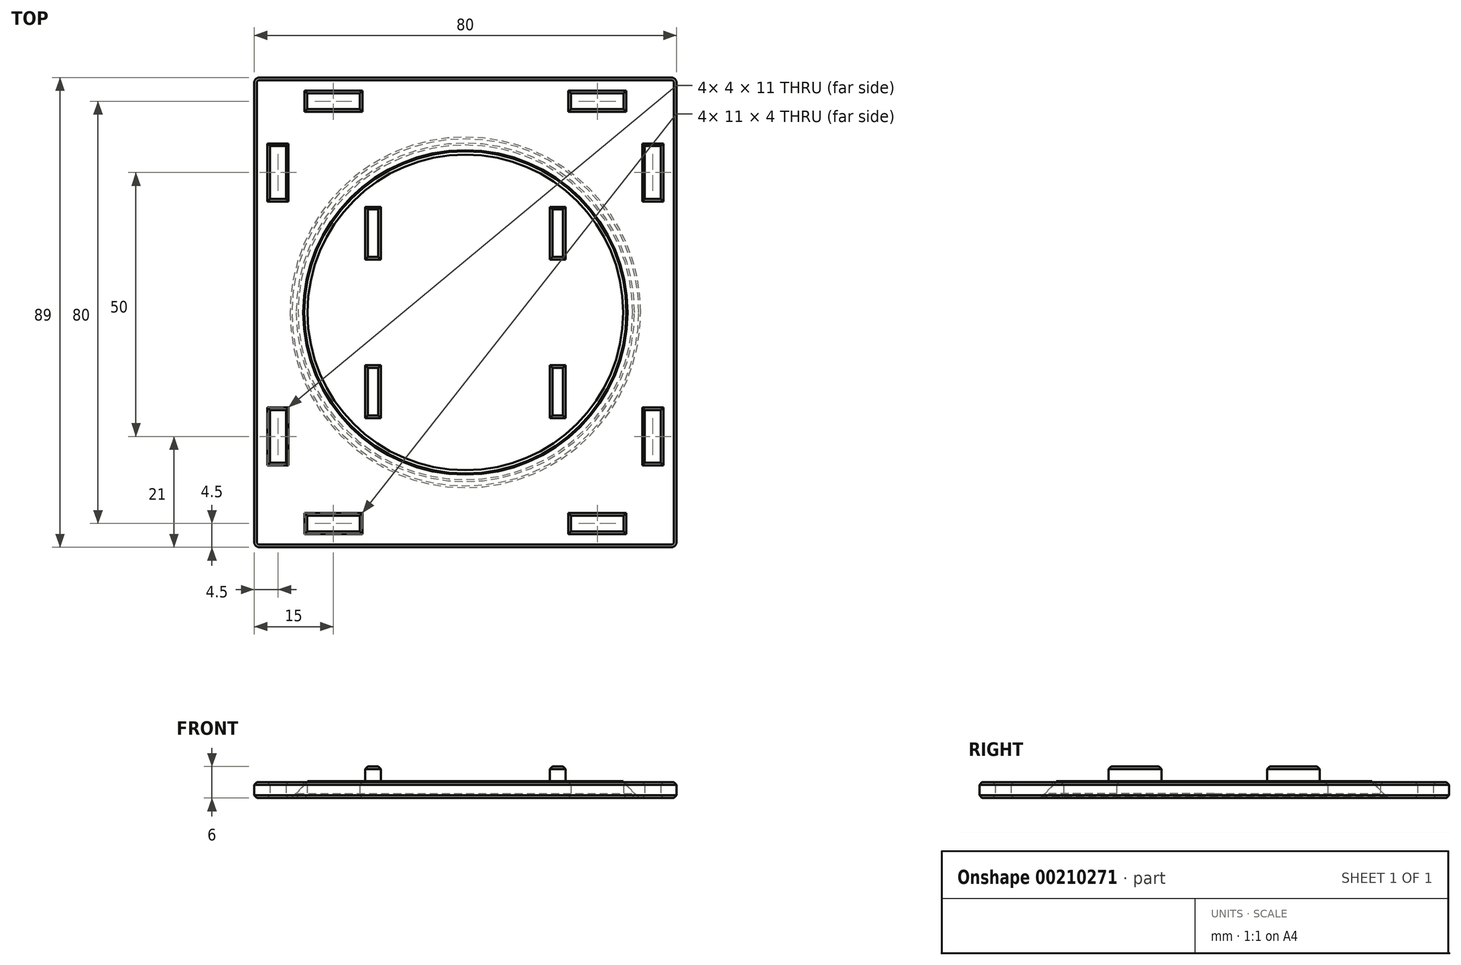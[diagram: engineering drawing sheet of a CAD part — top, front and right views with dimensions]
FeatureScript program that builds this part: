
annotation { "Feature Type Name" : "Feature", "Feature Type Description" : "" }
export const myFeature = defineFeature(function(context is Context, id is Id, definition is map)
    precondition{}
    {
        {
            var Q0;
            Q0=qCreatedBy(makeId("Top.planeOp"),FACE);
            var sketch = newSketch(context, id + "F0", { "sketchPlane" : qUnion([Q0])});
            skLineSegment(sketch, "E0.bottom", {"start": v(0, 0) * mm, "end": v(80, 0) * mm});
            skLineSegment(sketch, "E0.top", {"start": v(0, 89) * mm, "end": v(80, 89) * mm});
            skLineSegment(sketch, "E0.left", {"start": v(0, 0) * mm, "end": v(0, 89) * mm});
            skLineSegment(sketch, "E0.right", {"start": v(80, 0) * mm, "end": v(80, 89) * mm});
            skLineSegment(sketch, "E1.bottom", {"start": v(3, 76) * mm, "end": v(6, 76) * mm});
            skLineSegment(sketch, "E1.top", {"start": v(3, 66) * mm, "end": v(6, 66) * mm});
            skLineSegment(sketch, "E1.left", {"start": v(3, 76) * mm, "end": v(3, 66) * mm});
            skLineSegment(sketch, "E1.right", {"start": v(6, 76) * mm, "end": v(6, 66) * mm});
            skLineSegment(sketch, "E2.0.1.0", {"start": v(3, 26) * mm, "end": v(6, 26) * mm});
            skLineSegment(sketch, "E2.0.1.1", {"start": v(6, 26) * mm, "end": v(6, 16) * mm});
            skLineSegment(sketch, "E2.0.1.2", {"start": v(3, 26) * mm, "end": v(3, 16) * mm});
            skLineSegment(sketch, "E2.0.1.3", {"start": v(3, 16) * mm, "end": v(6, 16) * mm});
            skLineSegment(sketch, "E2.1.0.0", {"start": v(74, 76) * mm, "end": v(77, 76) * mm});
            skLineSegment(sketch, "E2.1.0.1", {"start": v(77, 76) * mm, "end": v(77, 66) * mm});
            skLineSegment(sketch, "E2.1.0.2", {"start": v(74, 76) * mm, "end": v(74, 66) * mm});
            skLineSegment(sketch, "E2.1.0.3", {"start": v(74, 66) * mm, "end": v(77, 66) * mm});
            skLineSegment(sketch, "E2.1.1.0", {"start": v(74, 26) * mm, "end": v(77, 26) * mm});
            skLineSegment(sketch, "E2.1.1.1", {"start": v(77, 26) * mm, "end": v(77, 16) * mm});
            skLineSegment(sketch, "E2.1.1.2", {"start": v(74, 26) * mm, "end": v(74, 16) * mm});
            skLineSegment(sketch, "E2.1.1.3", {"start": v(74, 16) * mm, "end": v(77, 16) * mm});
            skLineSegment(sketch, "E2.direction1", {"start": v(3, 76) * mm, "end": v(74, 76) * mm, "construction": true});
            skLineSegment(sketch, "E2.direction2", {"start": v(3, 76) * mm, "end": v(3, 26) * mm, "construction": true});
            skCircle(sketch, "E3", {"center": v(40, 44.5) * mm, "radius": 30 * mm});
            skPoint(sketch, "E3.centerSnap0", {"position": v(80, 44.5) * mm});
            skPoint(sketch, "E3.centerSnap1", {"position": v(40, 89) * mm});
            skLineSegment(sketch, "E4.bottom", {"start": v(70, 3) * mm, "end": v(60, 3) * mm});
            skLineSegment(sketch, "E4.top", {"start": v(70, 6) * mm, "end": v(60, 6) * mm});
            skLineSegment(sketch, "E4.left", {"start": v(70, 3) * mm, "end": v(70, 6) * mm});
            skLineSegment(sketch, "E4.right", {"start": v(60, 3) * mm, "end": v(60, 6) * mm});
            skLineSegment(sketch, "E5.0.1.0", {"start": v(70, 83) * mm, "end": v(60, 83) * mm});
            skLineSegment(sketch, "E5.0.1.1", {"start": v(60, 83) * mm, "end": v(60, 86) * mm});
            skLineSegment(sketch, "E5.0.1.2", {"start": v(70, 86) * mm, "end": v(60, 86) * mm});
            skLineSegment(sketch, "E5.0.1.3", {"start": v(70, 83) * mm, "end": v(70, 86) * mm});
            skLineSegment(sketch, "E5.1.0.0", {"start": v(20, 3) * mm, "end": v(10, 3) * mm});
            skLineSegment(sketch, "E5.1.0.1", {"start": v(10, 3) * mm, "end": v(10, 6) * mm});
            skLineSegment(sketch, "E5.1.0.2", {"start": v(20, 6) * mm, "end": v(10, 6) * mm});
            skLineSegment(sketch, "E5.1.0.3", {"start": v(20, 3) * mm, "end": v(20, 6) * mm});
            skLineSegment(sketch, "E5.1.1.0", {"start": v(20, 83) * mm, "end": v(10, 83) * mm});
            skLineSegment(sketch, "E5.1.1.1", {"start": v(10, 83) * mm, "end": v(10, 86) * mm});
            skLineSegment(sketch, "E5.1.1.2", {"start": v(20, 86) * mm, "end": v(10, 86) * mm});
            skLineSegment(sketch, "E5.1.1.3", {"start": v(20, 83) * mm, "end": v(20, 86) * mm});
            skLineSegment(sketch, "E5.direction1", {"start": v(60, 3) * mm, "end": v(10, 3) * mm, "construction": true});
            skLineSegment(sketch, "E5.direction2", {"start": v(60, 3) * mm, "end": v(60, 83) * mm, "construction": true});
            skSolve(sketch);
        }
        {
            var Q0;
            Q0=qSketchRegion(id+"F0",true);
            extrude(context, id + "F1", {"entities" : qUnion([Q0]), "depth" : 3 * mm});
        }
        {
            var Q0;
            Q0=makeQuery(id+"F1.opExtrude","CAP_EDGE",EDGE,{"disambiguationData":[OSD([sQuery(id+"F0.wireOp",EDGE,"E3")])],"isStart":true});
            chamfer(context, id + "F2", {"entities" : qUnion([Q0]), "width" : 3 * mm, "tangentPropagation" : true});
        }
        {
            var Q0;
            Q0=qCreatedBy(makeId("Top.planeOp"),FACE);
            var sketch = newSketch(context, id + "F3", { "sketchPlane" : qUnion([Q0])});
            skCircle(sketch, "E6", {"center": v(40, 44.5) * mm, "radius": 32.9 * mm});
            skSolve(sketch);
        }
        {
            var Q0;
            Q0=qSketchRegion(id+"F3",true);
            extrude(context, id + "F4", {"entities" : qUnion([Q0]), "depth" : 3 * mm});
        }
        {
            var Q0;
            Q0=makeQuery(id+"F4.opExtrude","CAP_EDGE",EDGE,{"disambiguationData":[OSD([sQuery(id+"F3.wireOp",EDGE,"E6")])],"isStart":false});
            chamfer(context, id + "F5", {"entities" : qUnion([Q0]), "width" : 3 * mm, "tangentPropagation" : true});
        }
        {
            var Q0;
            Q0=makeQuery(id+"F4.opExtrude","CAP_FACE",FACE,{"disambiguationData":[OSD([sQuery(id+"F3.wireOp",EDGE,"E6")])],"isStart":false});
            var sketch = newSketch(context, id + "F6", { "sketchPlane" : qUnion([Q0])});
            skCircle(sketch, "E7", {"center": v(40, 44.5) * mm, "radius": 29.9 * mm});
            skSolve(sketch);
        }
        {
            var Q0;
            Q0=qSketchRegion(id+"F6",true);
            extrude(context, id + "F7", {"entities" : qUnion([Q0]), "operationType" : NewBodyOperationType.ADD, "depth" : .2 * mm});
        }
        {
            var Q0;
            Q0=makeQuery(id+"F7.opExtrude","CAP_FACE",FACE,{"disambiguationData":[OSD([sQuery(id+"F6.wireOp",EDGE,"E7")])],"isStart":false});
            var sketch = newSketch(context, id + "F8", { "sketchPlane" : qUnion([Q0])});
            skLineSegment(sketch, "E8.bottom", {"start": v(24, 54.5) * mm, "end": v(21, 54.5) * mm});
            skLineSegment(sketch, "E8.top", {"start": v(24, 64.5) * mm, "end": v(21, 64.5) * mm});
            skLineSegment(sketch, "E8.left", {"start": v(24, 54.5) * mm, "end": v(24, 64.5) * mm});
            skLineSegment(sketch, "E8.right", {"start": v(21, 54.5) * mm, "end": v(21, 64.5) * mm});
            skLineSegment(sketch, "E9.0.1.0", {"start": v(24, 34.5) * mm, "end": v(21, 34.5) * mm});
            skLineSegment(sketch, "E9.0.1.1", {"start": v(24, 24.5) * mm, "end": v(24, 34.5) * mm});
            skLineSegment(sketch, "E9.0.1.2", {"start": v(21, 24.5) * mm, "end": v(21, 34.5) * mm});
            skLineSegment(sketch, "E9.0.1.3", {"start": v(24, 24.5) * mm, "end": v(21, 24.5) * mm});
            skLineSegment(sketch, "E9.1.0.0", {"start": v(59, 64.5) * mm, "end": v(56, 64.5) * mm});
            skLineSegment(sketch, "E9.1.0.1", {"start": v(59, 54.5) * mm, "end": v(59, 64.5) * mm});
            skLineSegment(sketch, "E9.1.0.2", {"start": v(56, 54.5) * mm, "end": v(56, 64.5) * mm});
            skLineSegment(sketch, "E9.1.0.3", {"start": v(59, 54.5) * mm, "end": v(56, 54.5) * mm});
            skLineSegment(sketch, "E9.1.1.0", {"start": v(59, 34.5) * mm, "end": v(56, 34.5) * mm});
            skLineSegment(sketch, "E9.1.1.1", {"start": v(59, 24.5) * mm, "end": v(59, 34.5) * mm});
            skLineSegment(sketch, "E9.1.1.2", {"start": v(56, 24.5) * mm, "end": v(56, 34.5) * mm});
            skLineSegment(sketch, "E9.1.1.3", {"start": v(59, 24.5) * mm, "end": v(56, 24.5) * mm});
            skLineSegment(sketch, "E9.direction1", {"start": v(21, 64.5) * mm, "end": v(56, 64.5) * mm, "construction": true});
            skLineSegment(sketch, "E9.direction2", {"start": v(21, 64.5) * mm, "end": v(21, 34.5) * mm, "construction": true});
            skSolve(sketch);
        }
        {
            var Q0;
            Q0=qSketchRegion(id+"F8",true);
            extrude(context, id + "F9", {"entities" : qUnion([Q0]), "operationType" : NewBodyOperationType.ADD, "depth" : 2.8 * mm});
        }
        {
            var Q0;
            Q0=makeQuery(id+"F1.opExtrude","SWEPT_EDGE",EDGE,{"disambiguationData":[OSD([sQuery(id+"F0.wireOp",EDGE,"E0.bottom"),sQuery(id+"F0.wireOp",EDGE,"E0.left")])]});
            var Q1;
            Q1=makeQuery(id+"F1.opExtrude","SWEPT_EDGE",EDGE,{"disambiguationData":[OSD([sQuery(id+"F0.wireOp",EDGE,"E0.bottom"),sQuery(id+"F0.wireOp",EDGE,"E0.right")])]});
            var Q2;
            Q2=makeQuery(id+"F1.opExtrude","SWEPT_EDGE",EDGE,{"disambiguationData":[OSD([sQuery(id+"F0.wireOp",EDGE,"E0.top"),sQuery(id+"F0.wireOp",EDGE,"E0.right")])]});
            var Q3;
            Q3=makeQuery(id+"F1.opExtrude","SWEPT_EDGE",EDGE,{"disambiguationData":[OSD([sQuery(id+"F0.wireOp",EDGE,"E0.top"),sQuery(id+"F0.wireOp",EDGE,"E0.left")])]});
            fillet(context, id + "F10", {"entities" : qUnion([Q0, Q1, Q2, Q3]), "radius" : 1 * mm, "tangentPropagation" : true, "allowEdgeOverflow" : false});
        }
        {
            var Q0;
            Q0=makeQuery(id+"F1.opExtrude","CAP_FACE",FACE,{"disambiguationData":[OSD([sQuery(id+"F0.wireOp",EDGE,"E0.bottom"),sQuery(id+"F0.wireOp",EDGE,"E0.top"),sQuery(id+"F0.wireOp",EDGE,"E0.left"),sQuery(id+"F0.wireOp",EDGE,"E0.right"),sQuery(id+"F0.wireOp",EDGE,"E1.bottom"),sQuery(id+"F0.wireOp",EDGE,"E1.top"),sQuery(id+"F0.wireOp",EDGE,"E1.left"),sQuery(id+"F0.wireOp",EDGE,"E1.right"),sQuery(id+"F0.wireOp",EDGE,"E2.0.1.0"),sQuery(id+"F0.wireOp",EDGE,"E2.0.1.1"),sQuery(id+"F0.wireOp",EDGE,"E2.0.1.2"),sQuery(id+"F0.wireOp",EDGE,"E2.0.1.3"),sQuery(id+"F0.wireOp",EDGE,"E2.1.0.0"),sQuery(id+"F0.wireOp",EDGE,"E2.1.0.1"),sQuery(id+"F0.wireOp",EDGE,"E2.1.0.2"),sQuery(id+"F0.wireOp",EDGE,"E2.1.0.3"),sQuery(id+"F0.wireOp",EDGE,"E2.1.1.0"),sQuery(id+"F0.wireOp",EDGE,"E2.1.1.1"),sQuery(id+"F0.wireOp",EDGE,"E2.1.1.2"),sQuery(id+"F0.wireOp",EDGE,"E2.1.1.3"),sQuery(id+"F0.wireOp",EDGE,"E3"),sQuery(id+"F0.wireOp",EDGE,"E4.bottom"),sQuery(id+"F0.wireOp",EDGE,"E4.top"),sQuery(id+"F0.wireOp",EDGE,"E4.left"),sQuery(id+"F0.wireOp",EDGE,"E4.right"),sQuery(id+"F0.wireOp",EDGE,"E5.0.1.0"),sQuery(id+"F0.wireOp",EDGE,"E5.0.1.1"),sQuery(id+"F0.wireOp",EDGE,"E5.0.1.2"),sQuery(id+"F0.wireOp",EDGE,"E5.0.1.3"),sQuery(id+"F0.wireOp",EDGE,"E5.1.0.0"),sQuery(id+"F0.wireOp",EDGE,"E5.1.0.1"),sQuery(id+"F0.wireOp",EDGE,"E5.1.0.2"),sQuery(id+"F0.wireOp",EDGE,"E5.1.0.3"),sQuery(id+"F0.wireOp",EDGE,"E5.1.1.0"),sQuery(id+"F0.wireOp",EDGE,"E5.1.1.1"),sQuery(id+"F0.wireOp",EDGE,"E5.1.1.2"),sQuery(id+"F0.wireOp",EDGE,"E5.1.1.3")])],"isStart":true});
            var Q1;
            Q1=makeQuery(id+"F4.opExtrude","CAP_FACE",FACE,{"disambiguationData":[OSD([sQuery(id+"F3.wireOp",EDGE,"E6")])],"isStart":true});
            chamfer(context, id + "F11", {"entities" : qUnion([Q0, Q1]), "width" : .5 * mm, "tangentPropagation" : true});
        }
        {
            var Q0;
            Q0=makeQuery(id+"F9.opExtrude","CAP_FACE",FACE,{"disambiguationData":[OSD([sQuery(id+"F8.wireOp",EDGE,"E8.bottom"),sQuery(id+"F8.wireOp",EDGE,"E8.top"),sQuery(id+"F8.wireOp",EDGE,"E8.left"),sQuery(id+"F8.wireOp",EDGE,"E8.right")])],"isStart":false});
            var Q1;
            Q1=makeQuery(id+"F9.opExtrude","CAP_FACE",FACE,{"disambiguationData":[OSD([sQuery(id+"F8.wireOp",EDGE,"E9.0.1.0"),sQuery(id+"F8.wireOp",EDGE,"E9.0.1.1"),sQuery(id+"F8.wireOp",EDGE,"E9.0.1.2"),sQuery(id+"F8.wireOp",EDGE,"E9.0.1.3")])],"isStart":false});
            var Q2;
            Q2=makeQuery(id+"F9.opExtrude","CAP_FACE",FACE,{"disambiguationData":[OSD([sQuery(id+"F8.wireOp",EDGE,"E9.1.1.0"),sQuery(id+"F8.wireOp",EDGE,"E9.1.1.1"),sQuery(id+"F8.wireOp",EDGE,"E9.1.1.2"),sQuery(id+"F8.wireOp",EDGE,"E9.1.1.3")])],"isStart":false});
            var Q3;
            Q3=makeQuery(id+"F9.opExtrude","CAP_FACE",FACE,{"disambiguationData":[OSD([sQuery(id+"F8.wireOp",EDGE,"E9.1.0.0"),sQuery(id+"F8.wireOp",EDGE,"E9.1.0.1"),sQuery(id+"F8.wireOp",EDGE,"E9.1.0.2"),sQuery(id+"F8.wireOp",EDGE,"E9.1.0.3")])],"isStart":false});
            chamfer(context, id + "F12", {"entities" : qUnion([Q0, Q1, Q2, Q3]), "width" : .5 * mm, "tangentPropagation" : true});
        }
        {
            var Q0;
            Q0=makeQuery(id+"F1.opExtrude","CAP_EDGE",EDGE,{"disambiguationData":[OSD([sQuery(id+"F0.wireOp",EDGE,"E0.right")])],"isStart":false});
            var Q1;
            Q1=makeQuery(id+"F1.opExtrude","CAP_EDGE",EDGE,{"disambiguationData":[OSD([sQuery(id+"F0.wireOp",EDGE,"E4.top")])],"isStart":false});
            var Q2;
            Q2=makeQuery(id+"F1.opExtrude","CAP_EDGE",EDGE,{"disambiguationData":[OSD([sQuery(id+"F0.wireOp",EDGE,"E4.left")])],"isStart":false});
            var Q3;
            Q3=makeQuery(id+"F1.opExtrude","CAP_EDGE",EDGE,{"disambiguationData":[OSD([sQuery(id+"F0.wireOp",EDGE,"E4.bottom")])],"isStart":false});
            var Q4;
            Q4=makeQuery(id+"F1.opExtrude","CAP_EDGE",EDGE,{"disambiguationData":[OSD([sQuery(id+"F0.wireOp",EDGE,"E4.right")])],"isStart":false});
            var Q5;
            Q5=makeQuery(id+"F1.opExtrude","CAP_EDGE",EDGE,{"disambiguationData":[OSD([sQuery(id+"F0.wireOp",EDGE,"E2.1.1.3")])],"isStart":false});
            var Q6;
            Q6=makeQuery(id+"F1.opExtrude","CAP_EDGE",EDGE,{"disambiguationData":[OSD([sQuery(id+"F0.wireOp",EDGE,"E2.1.1.2")])],"isStart":false});
            var Q7;
            Q7=makeQuery(id+"F1.opExtrude","CAP_EDGE",EDGE,{"disambiguationData":[OSD([sQuery(id+"F0.wireOp",EDGE,"E2.1.1.0")])],"isStart":false});
            var Q8;
            Q8=makeQuery(id+"F1.opExtrude","CAP_EDGE",EDGE,{"disambiguationData":[OSD([sQuery(id+"F0.wireOp",EDGE,"E2.1.1.1")])],"isStart":false});
            var Q9;
            Q9=makeQuery(id+"F1.opExtrude","CAP_EDGE",EDGE,{"disambiguationData":[OSD([sQuery(id+"F0.wireOp",EDGE,"E2.1.0.3")])],"isStart":false});
            var Q10;
            Q10=makeQuery(id+"F1.opExtrude","CAP_EDGE",EDGE,{"disambiguationData":[OSD([sQuery(id+"F0.wireOp",EDGE,"E2.1.0.2")])],"isStart":false});
            var Q11;
            Q11=makeQuery(id+"F1.opExtrude","CAP_EDGE",EDGE,{"disambiguationData":[OSD([sQuery(id+"F0.wireOp",EDGE,"E2.1.0.0")])],"isStart":false});
            var Q12;
            Q12=makeQuery(id+"F1.opExtrude","CAP_EDGE",EDGE,{"disambiguationData":[OSD([sQuery(id+"F0.wireOp",EDGE,"E2.1.0.1")])],"isStart":false});
            var Q13;
            Q13=makeQuery(id+"F1.opExtrude","CAP_EDGE",EDGE,{"disambiguationData":[OSD([sQuery(id+"F0.wireOp",EDGE,"E5.0.1.2")])],"isStart":false});
            var Q14;
            Q14=makeQuery(id+"F1.opExtrude","CAP_EDGE",EDGE,{"disambiguationData":[OSD([sQuery(id+"F0.wireOp",EDGE,"E5.0.1.0")])],"isStart":false});
            var Q15;
            Q15=makeQuery(id+"F1.opExtrude","CAP_EDGE",EDGE,{"disambiguationData":[OSD([sQuery(id+"F0.wireOp",EDGE,"E5.0.1.1")])],"isStart":false});
            var Q16;
            Q16=makeQuery(id+"F1.opExtrude","CAP_EDGE",EDGE,{"disambiguationData":[OSD([sQuery(id+"F0.wireOp",EDGE,"E5.0.1.3")])],"isStart":false});
            var Q17;
            Q17=makeQuery(id+"F1.opExtrude","CAP_EDGE",EDGE,{"disambiguationData":[OSD([sQuery(id+"F0.wireOp",EDGE,"E5.1.1.3")])],"isStart":false});
            var Q18;
            Q18=makeQuery(id+"F1.opExtrude","CAP_EDGE",EDGE,{"disambiguationData":[OSD([sQuery(id+"F0.wireOp",EDGE,"E5.1.1.1")])],"isStart":false});
            var Q19;
            Q19=makeQuery(id+"F1.opExtrude","CAP_EDGE",EDGE,{"disambiguationData":[OSD([sQuery(id+"F0.wireOp",EDGE,"E5.1.1.2")])],"isStart":false});
            var Q20;
            Q20=makeQuery(id+"F1.opExtrude","CAP_EDGE",EDGE,{"disambiguationData":[OSD([sQuery(id+"F0.wireOp",EDGE,"E5.1.1.0")])],"isStart":false});
            var Q21;
            Q21=makeQuery(id+"F1.opExtrude","CAP_EDGE",EDGE,{"disambiguationData":[OSD([sQuery(id+"F0.wireOp",EDGE,"E1.right")])],"isStart":false});
            var Q22;
            Q22=makeQuery(id+"F1.opExtrude","CAP_EDGE",EDGE,{"disambiguationData":[OSD([sQuery(id+"F0.wireOp",EDGE,"E1.left")])],"isStart":false});
            var Q23;
            Q23=makeQuery(id+"F1.opExtrude","CAP_EDGE",EDGE,{"disambiguationData":[OSD([sQuery(id+"F0.wireOp",EDGE,"E1.bottom")])],"isStart":false});
            var Q24;
            Q24=makeQuery(id+"F1.opExtrude","CAP_EDGE",EDGE,{"disambiguationData":[OSD([sQuery(id+"F0.wireOp",EDGE,"E1.top")])],"isStart":false});
            var Q25;
            Q25=makeQuery(id+"F1.opExtrude","CAP_EDGE",EDGE,{"disambiguationData":[OSD([sQuery(id+"F0.wireOp",EDGE,"E5.1.0.1")])],"isStart":false});
            var Q26;
            Q26=makeQuery(id+"F1.opExtrude","CAP_EDGE",EDGE,{"disambiguationData":[OSD([sQuery(id+"F0.wireOp",EDGE,"E5.1.0.0")])],"isStart":false});
            var Q27;
            Q27=makeQuery(id+"F1.opExtrude","CAP_EDGE",EDGE,{"disambiguationData":[OSD([sQuery(id+"F0.wireOp",EDGE,"E5.1.0.2")])],"isStart":false});
            var Q28;
            Q28=makeQuery(id+"F1.opExtrude","CAP_EDGE",EDGE,{"disambiguationData":[OSD([sQuery(id+"F0.wireOp",EDGE,"E5.1.0.3")])],"isStart":false});
            var Q29;
            Q29=makeQuery(id+"F1.opExtrude","CAP_EDGE",EDGE,{"disambiguationData":[OSD([sQuery(id+"F0.wireOp",EDGE,"E2.0.1.3")])],"isStart":false});
            var Q30;
            Q30=makeQuery(id+"F1.opExtrude","CAP_EDGE",EDGE,{"disambiguationData":[OSD([sQuery(id+"F0.wireOp",EDGE,"E2.0.1.0")])],"isStart":false});
            var Q31;
            Q31=makeQuery(id+"F1.opExtrude","CAP_EDGE",EDGE,{"disambiguationData":[OSD([sQuery(id+"F0.wireOp",EDGE,"E2.0.1.2")])],"isStart":false});
            var Q32;
            Q32=makeQuery(id+"F1.opExtrude","CAP_EDGE",EDGE,{"disambiguationData":[OSD([sQuery(id+"F0.wireOp",EDGE,"E2.0.1.1")])],"isStart":false});
            chamfer(context, id + "F13", {"entities" : qUnion([Q0, Q1, Q2, Q3, Q4, Q5, Q6, Q7, Q8, Q9, Q10, Q11, Q12, Q13, Q14, Q15, Q16, Q17, Q18, Q19, Q20, Q21, Q22, Q23, Q24, Q25, Q26, Q27, Q28, Q29, Q30, Q31, Q32]), "width" : .5 * mm, "tangentPropagation" : true});
        }
        {
            var Q0;
            {var subQ0=sQuery(id+"F0.wireOp",EDGE,"E3");Q0=makeQuery(id+"F2.opChamfer","BLEND_EDGE",EDGE,{"blendedFrom":[makeQuery(id+"F1.opExtrude","CAP_EDGE",EDGE,{"disambiguationData":[OSD([subQ0])],"isStart":true}),makeQuery(id+"F1.opExtrude","CAP_FACE",FACE,{"disambiguationData":[OSD([sQuery(id+"F0.wireOp",EDGE,"E0.bottom"),sQuery(id+"F0.wireOp",EDGE,"E0.top"),sQuery(id+"F0.wireOp",EDGE,"E0.left"),sQuery(id+"F0.wireOp",EDGE,"E0.right"),sQuery(id+"F0.wireOp",EDGE,"E1.bottom"),sQuery(id+"F0.wireOp",EDGE,"E1.top"),sQuery(id+"F0.wireOp",EDGE,"E1.left"),sQuery(id+"F0.wireOp",EDGE,"E1.right"),sQuery(id+"F0.wireOp",EDGE,"E2.0.1.0"),sQuery(id+"F0.wireOp",EDGE,"E2.0.1.1"),sQuery(id+"F0.wireOp",EDGE,"E2.0.1.2"),sQuery(id+"F0.wireOp",EDGE,"E2.0.1.3"),sQuery(id+"F0.wireOp",EDGE,"E2.1.0.0"),sQuery(id+"F0.wireOp",EDGE,"E2.1.0.1"),sQuery(id+"F0.wireOp",EDGE,"E2.1.0.2"),sQuery(id+"F0.wireOp",EDGE,"E2.1.0.3"),sQuery(id+"F0.wireOp",EDGE,"E2.1.1.0"),sQuery(id+"F0.wireOp",EDGE,"E2.1.1.1"),sQuery(id+"F0.wireOp",EDGE,"E2.1.1.2"),sQuery(id+"F0.wireOp",EDGE,"E2.1.1.3"),subQ0,sQuery(id+"F0.wireOp",EDGE,"E4.bottom"),sQuery(id+"F0.wireOp",EDGE,"E4.top"),sQuery(id+"F0.wireOp",EDGE,"E4.left"),sQuery(id+"F0.wireOp",EDGE,"E4.right"),sQuery(id+"F0.wireOp",EDGE,"E5.0.1.0"),sQuery(id+"F0.wireOp",EDGE,"E5.0.1.1"),sQuery(id+"F0.wireOp",EDGE,"E5.0.1.2"),sQuery(id+"F0.wireOp",EDGE,"E5.0.1.3"),sQuery(id+"F0.wireOp",EDGE,"E5.1.0.0"),sQuery(id+"F0.wireOp",EDGE,"E5.1.0.1"),sQuery(id+"F0.wireOp",EDGE,"E5.1.0.2"),sQuery(id+"F0.wireOp",EDGE,"E5.1.0.3"),sQuery(id+"F0.wireOp",EDGE,"E5.1.1.0"),sQuery(id+"F0.wireOp",EDGE,"E5.1.1.1"),sQuery(id+"F0.wireOp",EDGE,"E5.1.1.2"),sQuery(id+"F0.wireOp",EDGE,"E5.1.1.3")])],"isStart":false})],"blendedInto":[makeQuery(id+"F1.opExtrude","CAP_FACE",FACE,{"disambiguationData":[OSD([sQuery(id+"F0.wireOp",EDGE,"E0.bottom"),sQuery(id+"F0.wireOp",EDGE,"E0.top"),sQuery(id+"F0.wireOp",EDGE,"E0.left"),sQuery(id+"F0.wireOp",EDGE,"E0.right"),sQuery(id+"F0.wireOp",EDGE,"E1.bottom"),sQuery(id+"F0.wireOp",EDGE,"E1.top"),sQuery(id+"F0.wireOp",EDGE,"E1.left"),sQuery(id+"F0.wireOp",EDGE,"E1.right"),sQuery(id+"F0.wireOp",EDGE,"E2.0.1.0"),sQuery(id+"F0.wireOp",EDGE,"E2.0.1.1"),sQuery(id+"F0.wireOp",EDGE,"E2.0.1.2"),sQuery(id+"F0.wireOp",EDGE,"E2.0.1.3"),sQuery(id+"F0.wireOp",EDGE,"E2.1.0.0"),sQuery(id+"F0.wireOp",EDGE,"E2.1.0.1"),sQuery(id+"F0.wireOp",EDGE,"E2.1.0.2"),sQuery(id+"F0.wireOp",EDGE,"E2.1.0.3"),sQuery(id+"F0.wireOp",EDGE,"E2.1.1.0"),sQuery(id+"F0.wireOp",EDGE,"E2.1.1.1"),sQuery(id+"F0.wireOp",EDGE,"E2.1.1.2"),sQuery(id+"F0.wireOp",EDGE,"E2.1.1.3"),subQ0,sQuery(id+"F0.wireOp",EDGE,"E4.bottom"),sQuery(id+"F0.wireOp",EDGE,"E4.top"),sQuery(id+"F0.wireOp",EDGE,"E4.left"),sQuery(id+"F0.wireOp",EDGE,"E4.right"),sQuery(id+"F0.wireOp",EDGE,"E5.0.1.0"),sQuery(id+"F0.wireOp",EDGE,"E5.0.1.1"),sQuery(id+"F0.wireOp",EDGE,"E5.0.1.2"),sQuery(id+"F0.wireOp",EDGE,"E5.0.1.3"),sQuery(id+"F0.wireOp",EDGE,"E5.1.0.0"),sQuery(id+"F0.wireOp",EDGE,"E5.1.0.1"),sQuery(id+"F0.wireOp",EDGE,"E5.1.0.2"),sQuery(id+"F0.wireOp",EDGE,"E5.1.0.3"),sQuery(id+"F0.wireOp",EDGE,"E5.1.1.0"),sQuery(id+"F0.wireOp",EDGE,"E5.1.1.1"),sQuery(id+"F0.wireOp",EDGE,"E5.1.1.2"),sQuery(id+"F0.wireOp",EDGE,"E5.1.1.3")])],"isStart":false})]});}
            chamfer(context, id + "F14", {"entities" : qUnion([Q0]), "width" : .3 * mm, "tangentPropagation" : true});
        }
    });
